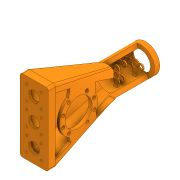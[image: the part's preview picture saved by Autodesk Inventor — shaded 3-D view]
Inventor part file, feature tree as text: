
AUTODESK INVENTOR PART (.ipt)
format: ipt  version: 2020 (Build 240168000, 168)  size: 1,076,736 bytes
history: native  units: in
note: dims shown in document units (in); Inventor stores cm internally (conversion verified against a paired STEP export)
features: chamfer x23, sketch x19, extrude x16, projected_geometry x9, plane x3, loft x2, fillet x1, other x1
ambient origin geometry x8: Origin, YZ Plane, XZ Plane, XY Plane, X Axis, Y Axis, Z Axis, Center Point
bodies: Solid1 (feature_tree)
feature tree (74):
  extrude  "Extrusion1"  Depth=2.0472in
  extrude  "Extrusion2"  Depth=1.6535in
  chamfer  "Chamfer1"  Distance=0.5512in
  extrude  "Extrusion3"  Depth=0.0157in
  extrude  "Extrusion4"  Depth=0.2756in TaperAngle=0.0deg
  extrude  "Extrusion5"  Depth=0.315in
  extrude  "Extrusion6"  Depth=0.4724in
  extrude  "Extrusion7"  Depth=0.0787in
  plane  "Work Plane1"
  extrude  "Extrusion8"  Depth=0.1575in
  plane  "Work Plane2"
  extrude  "Extrusion9"  Depth=1.0994in
  sketch  "Sketch11"  dims[d31=15.0deg d32=0.4921in d33=0.0in]
  plane  "Work Plane3"
  extrude  "Extrusion10"  Depth=0.4921in TaperAngle=0.0deg
  extrude  "Extrusion11"  Depth=1.5748in TaperAngle=360.0deg
  loft  "Loft1"
  loft  "Loft2"
  sketch  "Sketch16"  dims[d47=0.315in d48=0.4331in]
  extrude  "Extrusion12"  Depth=0.0984in TaperAngle=0.0deg
  extrude  "Extrusion13"  Depth=0.4331in
  extrude  "Extrusion14"  Depth=0.6161in
  extrude  "Extrusion15"  Depth=0.1575in
  chamfer  "Chamfer2"  Distance=0.0984in
  chamfer  "Chamfer3"  Distance=1.6654in
  chamfer  "Chamfer4"  Distance=1.6654in
  chamfer  "Chamfer5"  [1 undecoded]
  chamfer  "Chamfer6"  [1 undecoded]
  chamfer  "Chamfer7"  Distance=1.6654in
  chamfer  "Chamfer8"  Distance=1.6654in
  chamfer  "Chamfer9"  Distance=0.1969in
  chamfer  "Chamfer10"  Distance=0.1969in
  chamfer  "Chamfer11"  Distance=0.3484in
  chamfer  "Chamfer12"  Distance=0.3484in
  chamfer  "Chamfer13"  Distance=0.1969in
  chamfer  "Chamfer14"  Distance=0.1969in
  chamfer  "Chamfer15"  Distance=0.1969in
  chamfer  "Chamfer16"  Distance=0.3937in
  chamfer  "Chamfer17"  Distance=0.7874in
  chamfer  "Chamfer18"  Angle=90.0deg  [1 undecoded]
  chamfer  "Chamfer19"  Angle=90.0deg  [1 undecoded]
  chamfer  "Chamfer20"  Angle=90.0deg  [1 undecoded]
  chamfer  "Chamfer21"  Angle=90.0deg  [1 undecoded]
  chamfer  "Chamfer22"  Distance=0.7874in
  fillet  "Fillet1"  Radius=0.3937in
  chamfer  "Chamfer23"  Distance=0.3937in
  extrude  "Extrusion19"  Depth=0.3937in TaperAngle=0.0deg
  sketch  "Sketch1"  dims[d0=2.3622in d1=2.0472in]
  sketch  "Sketch2"  dims[d2=0.2756in d3=0.0in d4=1.6535in d5=0.5512in d6=0.0in]
  sketch  "Sketch3"  dims[d7=0.2756in d8=0.125in d9=0.0137in d10=0.0157in]
  sketch  "Sketch5"  dims[d11=4.7244in d13=360.0deg d15=0.2756in d16=0.0in]
  sketch  "Sketch6"  dims[d17=0.5512in d19=0.315in]
  projected_geometry  "Projected Loop1"
  sketch  "Sketch7"  dims[d20=0.315in d21=0.4724in]
  projected_geometry  "Projected Loop2"
  sketch  "Sketch8"  dims[d22=0.4724in d23=0.0787in d24=0.0787in d25=0.0787in]
  projected_geometry  "Projected Loop3"
  sketch  "Sketch9"  dims[d26=0.0984in d27=0.0in d28=0.1575in]
  sketch  "Sketch10"  dims[d29=0.1575in d30=1.0994in]
  sketch  "Sketch12"  dims[d34=1.4567in d35=0.0in d36=1.5748in d38=360.0deg]
  sketch  "Sketch13"  dims[d40=0.0787in d41=0.0787in]
  projected_geometry  "Projected Loop4"
  other  "Edges1"
  sketch  "Sketch14"  dims[d42=0.0787in d43=0.0787in]
  projected_geometry  "Projected Loop5"
  sketch  "Sketch15"  dims[d44=0.0787in d45=0.0984in d46=0.0in]
  projected_geometry  "Projected Loop6"
  projected_geometry  "Projected Loop7"
  sketch  "Sketch19"  dims[d49=0.0984in d50=0.0in d51=0.6161in]
  projected_geometry  "Projected Loop8"
  sketch  "Sketch20"  dims[d52=0.1575in d53=0.1575in d54=0.0984in d55=0.0in]
  projected_geometry  "Projected Loop9"
  sketch  "Sketch21"  dims[d56=6.6929in]
  sketch  "Sketch25"  dims[d57=0.8858in d58=1.6654in d59=1.6654in d60=0.0in d61=0.0in d62=1.6654in d63=1.6654in d64=0.1969in d65=0.1969in d66=0.3484in d67=0.3484in d68=0.1969in d69=0.1969in d70=0.1969in d71=0.3937in d72=0.0in d73=0.7874in d74=0.0in d75=0.0in d76=90.0deg d77=0.0in d78=90.0deg d79=0.0in d80=90.0deg d81=0.0in d82=90.0deg d86=0.7874in d87=0.0in d90=0.3937in d91=0.3937in d92=0.7874in d93=0.0in d94=0.1969in d95=0.0in d96=0.8858in d97=1.6654in d98=1.6654in d99=0.0in d100=0.0in d101=0.2224in d102=0.1575in d103=0.1575in d104=0.1575in d105=0.1575in d106=0.0984in d107=0.0984in d108=0.1969in d109=0.0in d122=0.1575in d123=0.0787in d124=45.0deg d125=0.0787in d126=0.1575in d127=45.0deg d128=0.1575in d129=0.0787in d130=45.0deg d131=0.0787in d132=0.1575in d133=45.0deg d134=0.1575in d135=0.0787in d136=45.0deg d137=0.1575in d138=0.0787in d139=45.0deg d140=0.1575in d141=0.0787in d142=45.0deg d143=0.1575in d144=0.0787in d145=45.0deg d146=0.0787in d147=0.1575in d148=45.0deg d149=0.1575in d150=0.0787in d151=45.0deg d152=0.1575in d153=0.0787in d154=45.0deg d155=0.0787in d156=0.1575in d157=45.0deg d158=0.0591in d159=0.1575in d160=0.0137in d161=0.0591in d162=0.1575in d163=0.0137in d164=0.0591in d165=0.1575in d166=0.0137in d167=0.0591in d168=0.1575in d169=0.0137in d170=0.0591in d171=0.1575in d172=0.0137in d173=0.0591in d174=0.1575in d175=0.0137in d176=0.0591in d177=0.1575in d178=0.0137in d179=0.0591in d180=0.1575in d181=0.0137in d182=0.0591in d183=0.1575in d184=0.0137in d185=0.0197in d193=0.0984in d194=0.3937in d195=0.125in d196=45.0deg d197=0.2756in d198=0.1969in d199=0.0in d200=0.2756in d201=2.7559in d202=0.2756in d203=0.2756in d204=0.2756in d205=0.2756in d206=0.2756in d207=0.2756in d208=0.2756in d209=0.0394in d210=0.5in d211=0.0344in d212=0.5in d213=0.0344in]
note: 6 required parameter values undecoded (feature->parameter linkage not recoverable at this tier; creation-order binding heuristic only, values carry confidence <= 0.55)
